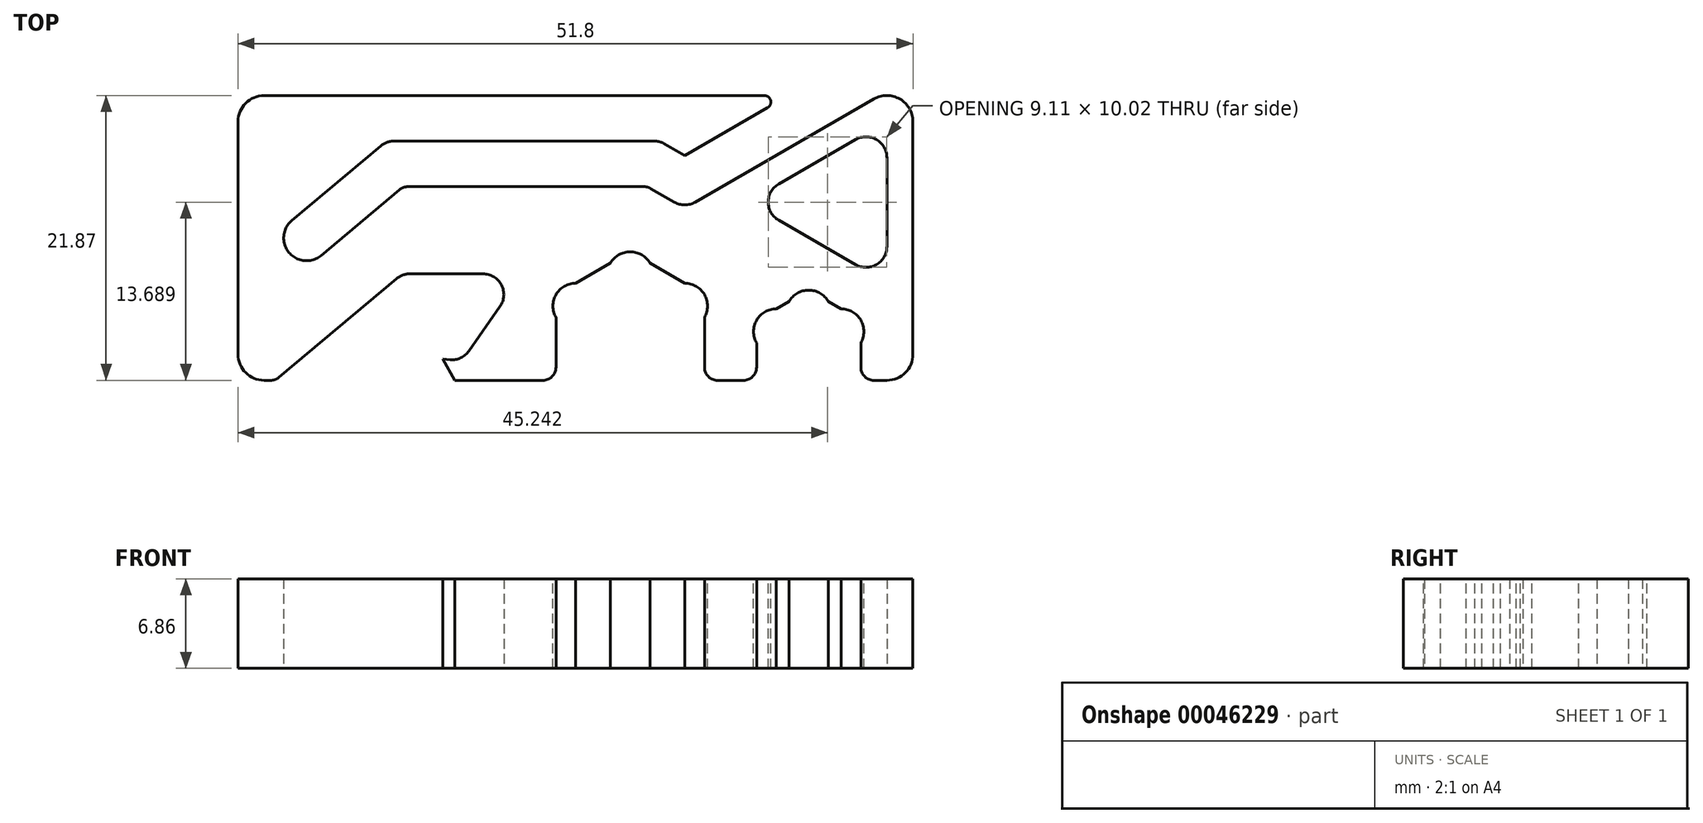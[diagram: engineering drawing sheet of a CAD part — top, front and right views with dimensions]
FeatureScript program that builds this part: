
annotation { "Feature Type Name" : "Feature", "Feature Type Description" : "" }
export const myFeature = defineFeature(function(context is Context, id is Id, definition is map)
    precondition{}
    {
        {
            var Q0;
            Q0=qCreatedBy(makeId("Top.planeOp"),FACE);
            var sketch = newSketch(context, id + "F0", { "sketchPlane" : qUnion([Q0])});
            skLineSegment(sketch, "E0", {"start": v(2, 0) * mm, "end": v(2.5, 0) * mm});
            skLineSegment(sketch, "E1", {"start": v(3.14, 0.23) * mm, "end": v(12.61, 8.18) * mm});
            skLineSegment(sketch, "E2", {"start": v(12.61, 8.18) * mm, "end": v(18.8, 8.18) * mm});
            skLineSegment(sketch, "E3", {"start": v(24.4, 0) * mm, "end": v(16.64, 0) * mm});
            skLineSegment(sketch, "E4", {"start": v(16.64, 0) * mm, "end": v(15.7, 1.63) * mm});
            skLineSegment(sketch, "E5", {"start": v(15.7, 1.63) * mm, "end": v(17.2, 1.5) * mm});
            skLineSegment(sketch, "E6", {"start": v(17.2, 1.5) * mm, "end": v(20.1, 5.66) * mm});
            skArc(sketch, "E7", {"start": v(20.1, 5.66) * mm, "mid": v(20.22, 7.32) * mm, "end": v(18.8, 8.18) * mm});
            skLineSegment(sketch, "E8", {"start": v(24.4, 0) * mm, "end": v(24.4, 6.58) * mm});
            skLineSegment(sketch, "E9", {"start": v(24.4, 6.58) * mm, "end": v(30.1, 9.87) * mm});
            skLineSegment(sketch, "E10", {"start": v(30.1, 9.87) * mm, "end": v(35.8, 6.58) * mm});
            skLineSegment(sketch, "E11", {"start": v(35.8, 6.58) * mm, "end": v(35.8, 0) * mm});
            skCircle(sketch, "E12", {"center": v(30.1, 3.3) * mm, "radius": 5.7 * mm, "construction": true});
            skLineSegment(sketch, "E13", {"start": v(18.8, 6.58) * mm, "end": v(20.4, 6.58) * mm, "construction": true});
            skArc(sketch, "E14", {"start": v(2.5, 0) * mm, "mid": v(2.84, 0.06) * mm, "end": v(3.14, 0.23) * mm});
            skLineSegment(sketch, "E15", {"start": v(0, 2) * mm, "end": v(0, 21.87) * mm});
            skArc(sketch, "E16", {"start": v(0, 2) * mm, "mid": v(0.59, 0.59) * mm, "end": v(2, 0) * mm});
            skLineSegment(sketch, "E17", {"start": v(35.8, 0) * mm, "end": v(39.8, 0) * mm});
            skLineSegment(sketch, "E18", {"start": v(39.8, 0) * mm, "end": v(39.8, 4.62) * mm});
            skLineSegment(sketch, "E19", {"start": v(39.8, 4.62) * mm, "end": v(43.8, 6.93) * mm});
            skLineSegment(sketch, "E20", {"start": v(43.8, 6.93) * mm, "end": v(47.8, 4.62) * mm});
            skLineSegment(sketch, "E21", {"start": v(47.8, 4.62) * mm, "end": v(47.8, 0) * mm});
            skLineSegment(sketch, "E22", {"start": v(47.8, 0) * mm, "end": v(51.8, 0) * mm});
            skCircle(sketch, "E23", {"center": v(43.8, 2.3) * mm, "radius": 4 * mm, "construction": true});
            skLineSegment(sketch, "E24", {"start": v(39.09, 13.69) * mm, "end": v(49.8, 7.5) * mm});
            skLineSegment(sketch, "E25", {"start": v(49.8, 7.5) * mm, "end": v(49.8, 19.87) * mm});
            skLineSegment(sketch, "E26", {"start": v(49.8, 19.87) * mm, "end": v(39.09, 13.69) * mm});
            skLineSegment(sketch, "E27", {"start": v(51.8, 0) * mm, "end": v(51.8, 19.87) * mm});
            skLineSegment(sketch, "E28", {"start": v(6.37, 9.6) * mm, "end": v(12.66, 14.87) * mm});
            skLineSegment(sketch, "E29", {"start": v(12.66, 14.87) * mm, "end": v(30.1, 14.87) * mm});
            skArc(sketch, "E30", {"start": v(4.13, 12.28) * mm, "mid": v(3.9, 9.81) * mm, "end": v(6.37, 9.6) * mm});
            skLineSegment(sketch, "E31", {"start": v(4.13, 12.28) * mm, "end": v(11.39, 18.37) * mm});
            skPoint(sketch, "E32", {"position": v(3.5, 10.94) * mm});
            skLineSegment(sketch, "E33", {"start": v(11.39, 18.37) * mm, "end": v(32.37, 18.37) * mm});
            skLineSegment(sketch, "E34", {"start": v(30.1, 14.87) * mm, "end": v(31.44, 14.87) * mm});
            skLineSegment(sketch, "E35", {"start": v(31.44, 14.87) * mm, "end": v(34.29, 13.23) * mm});
            skLineSegment(sketch, "E36", {"start": v(34.29, 13.23) * mm, "end": v(48.8, 21.6) * mm});
            skLineSegment(sketch, "E37", {"start": v(42.26, 21.87) * mm, "end": v(34.29, 17.27) * mm});
            skLineSegment(sketch, "E38", {"start": v(34.29, 17.27) * mm, "end": v(32.37, 18.37) * mm});
            skLineSegment(sketch, "E39", {"start": v(42.26, 21.87) * mm, "end": v(0, 21.87) * mm});
            skLineSegment(sketch, "E40", {"start": v(0, 0) * mm, "end": v(0, 21.87) * mm, "construction": true});
            skPoint(sketch, "E41", {"position": v(0, 10.94) * mm});
            skArc(sketch, "E42", {"start": v(51.8, 19.87) * mm, "mid": v(50.8, 21.6) * mm, "end": v(48.8, 21.6) * mm});
            skSolve(sketch);
        }
        {
            var Q0;
            Q0=makeQuery(id+"F0.imprint","IMPRINT",FACE,{"disambiguationData":[TD([[makeQuery(id+"F0.imprint","IMPRINT",EDGE,{"derivedFrom":sQuery(id+"F0.wireOp",EDGE,"E0")}),1.0]])]});
            extrude(context, id + "F1", {"entities" : qUnion([Q0]), "depth" : 6.86 * mm});
        }
        {
            var Q0;
            Q0=makeQuery(id+"F1.opExtrude","CAP_FACE",FACE,{"disambiguationData":[OSD([sQuery(id+"F0.wireOp",EDGE,"E0"),sQuery(id+"F0.wireOp",EDGE,"E1"),sQuery(id+"F0.wireOp",EDGE,"E2"),sQuery(id+"F0.wireOp",EDGE,"E3"),sQuery(id+"F0.wireOp",EDGE,"E4"),sQuery(id+"F0.wireOp",EDGE,"E5"),sQuery(id+"F0.wireOp",EDGE,"E6"),sQuery(id+"F0.wireOp",EDGE,"E7"),sQuery(id+"F0.wireOp",EDGE,"E8"),sQuery(id+"F0.wireOp",EDGE,"E9"),sQuery(id+"F0.wireOp",EDGE,"E10"),sQuery(id+"F0.wireOp",EDGE,"E11"),sQuery(id+"F0.wireOp",EDGE,"E14"),sQuery(id+"F0.wireOp",EDGE,"E15"),sQuery(id+"F0.wireOp",EDGE,"E16"),sQuery(id+"F0.wireOp",EDGE,"E17"),sQuery(id+"F0.wireOp",EDGE,"E18"),sQuery(id+"F0.wireOp",EDGE,"E19"),sQuery(id+"F0.wireOp",EDGE,"E20"),sQuery(id+"F0.wireOp",EDGE,"E21"),sQuery(id+"F0.wireOp",EDGE,"E22"),sQuery(id+"F0.wireOp",EDGE,"E24"),sQuery(id+"F0.wireOp",EDGE,"E25"),sQuery(id+"F0.wireOp",EDGE,"E26"),sQuery(id+"F0.wireOp",EDGE,"E27"),sQuery(id+"F0.wireOp",EDGE,"E28"),sQuery(id+"F0.wireOp",EDGE,"E29"),sQuery(id+"F0.wireOp",EDGE,"E30"),sQuery(id+"F0.wireOp",EDGE,"E31"),sQuery(id+"F0.wireOp",EDGE,"E33"),sQuery(id+"F0.wireOp",EDGE,"E34"),sQuery(id+"F0.wireOp",EDGE,"E35"),sQuery(id+"F0.wireOp",EDGE,"E36"),sQuery(id+"F0.wireOp",EDGE,"E37"),sQuery(id+"F0.wireOp",EDGE,"E38"),sQuery(id+"F0.wireOp",EDGE,"E39"),sQuery(id+"F0.wireOp",EDGE,"E42")])],"isStart":false});
            var sketch = newSketch(context, id + "F2", { "sketchPlane" : qUnion([Q0])});
            skLineSegment(sketch, "E43", {"start": v(30.1, 9.87) * mm, "end": v(30.1, 3.3) * mm, "construction": true});
            skLineSegment(sketch, "E44", {"start": v(30.1, 3.3) * mm, "end": v(24.4, 6.58) * mm, "construction": true});
            skLineSegment(sketch, "E45", {"start": v(30.1, 3.3) * mm, "end": v(35.8, 6.58) * mm, "construction": true});
            skCircle(sketch, "E46", {"center": v(30.1, 8.12) * mm, "radius": 1.75 * mm});
            skCircle(sketch, "E47", {"center": v(34.28, 5.7) * mm, "radius": 1.75 * mm});
            skCircle(sketch, "E48", {"center": v(25.91, 5.7) * mm, "radius": 1.75 * mm});
            skLineSegment(sketch, "E49", {"start": v(43.8, 6.93) * mm, "end": v(43.8, 2.3) * mm, "construction": true});
            skLineSegment(sketch, "E50", {"start": v(43.8, 2.3) * mm, "end": v(39.8, 4.62) * mm, "construction": true});
            skLineSegment(sketch, "E51", {"start": v(43.8, 2.3) * mm, "end": v(47.8, 4.62) * mm, "construction": true});
            skCircle(sketch, "E52", {"center": v(43.8, 5.18) * mm, "radius": 1.75 * mm});
            skCircle(sketch, "E53", {"center": v(46.28, 3.74) * mm, "radius": 1.75 * mm});
            skCircle(sketch, "E54", {"center": v(41.31, 3.74) * mm, "radius": 1.75 * mm});
            skLineSegment(sketch, "E55", {"start": v(21.88, 18.37) * mm, "end": v(21.88, 14.87) * mm, "construction": true});
            skLineSegment(sketch, "E56", {"start": v(28.35, 8.12) * mm, "end": v(31.85, 8.12) * mm, "construction": true});
            skSolve(sketch);
        }
        {
            var Q0;
            Q0 = qSketchRegion(id + "F2", true);
            extrude(context, id + "F3", {"entities" : qUnion([Q0]), "operationType" : NewBodyOperationType.REMOVE, "endBound" : BoundingType.THROUGH_ALL, "oppositeDirection" : true, "depth" : 25 * mm});
        }
        {
            var Q0;
            Q0=makeQuery(id+"F1.opExtrude","SWEPT_EDGE",EDGE,{"disambiguationData":[OSD([sQuery(id+"F0.wireOp",EDGE,"E3"),sQuery(id+"F0.wireOp",EDGE,"E8")])]});
            var Q1;
            Q1=makeQuery(id+"F1.opExtrude","SWEPT_EDGE",EDGE,{"disambiguationData":[OSD([sQuery(id+"F0.wireOp",EDGE,"E11"),sQuery(id+"F0.wireOp",EDGE,"E17")])]});
            var Q2;
            Q2=makeQuery(id+"F1.opExtrude","SWEPT_EDGE",EDGE,{"disambiguationData":[OSD([sQuery(id+"F0.wireOp",EDGE,"E17"),sQuery(id+"F0.wireOp",EDGE,"E18")])]});
            var Q3;
            Q3=makeQuery(id+"F1.opExtrude","SWEPT_EDGE",EDGE,{"disambiguationData":[OSD([sQuery(id+"F0.wireOp",EDGE,"E21"),sQuery(id+"F0.wireOp",EDGE,"E22")])]});
            fillet(context, id + "F4", {"entities" : qUnion([Q0, Q1, Q2, Q3]), "radius" : 1 * mm, "tangentPropagation" : true, "allowEdgeOverflow" : false});
        }
        {
            var Q0;
            Q0=makeQuery(id+"F1.opExtrude","SWEPT_EDGE",EDGE,{"disambiguationData":[OSD([sQuery(id+"F0.wireOp",EDGE,"E22"),sQuery(id+"F0.wireOp",EDGE,"E27")])]});
            var Q1;
            Q1=makeQuery(id+"F1.opExtrude","SWEPT_EDGE",EDGE,{"disambiguationData":[OSD([sQuery(id+"F0.wireOp",EDGE,"E15"),sQuery(id+"F0.wireOp",EDGE,"E39")])]});
            fillet(context, id + "F5", {"entities" : qUnion([Q0, Q1]), "radius" : 2 * mm, "tangentPropagation" : true, "allowEdgeOverflow" : false});
        }
        {
            var Q0;
            Q0=makeQuery(id+"F1.opExtrude","SWEPT_EDGE",EDGE,{"disambiguationData":[OSD([sQuery(id+"F0.wireOp",EDGE,"E37"),sQuery(id+"F0.wireOp",EDGE,"E39")])]});
            fillet(context, id + "F6", {"entities" : qUnion([Q0]), "radius" : 0.5 * mm, "tangentPropagation" : true, "allowEdgeOverflow" : false});
        }
        {
            var Q0;
            Q0=makeQuery(id+"F1.opExtrude","SWEPT_EDGE",EDGE,{"disambiguationData":[OSD([sQuery(id+"F0.wireOp",EDGE,"E28"),sQuery(id+"F0.wireOp",EDGE,"E29")])]});
            var Q1;
            Q1=makeQuery(id+"F1.opExtrude","SWEPT_EDGE",EDGE,{"disambiguationData":[OSD([sQuery(id+"F0.wireOp",EDGE,"E34"),sQuery(id+"F0.wireOp",EDGE,"E35")])]});
            fillet(context, id + "F7", {"entities" : qUnion([Q0, Q1]), "radius" : 1 * mm, "tangentPropagation" : true, "allowEdgeOverflow" : false});
        }
        {
            var Q0;
            Q0=makeQuery(id+"F1.opExtrude","SWEPT_EDGE",EDGE,{"disambiguationData":[OSD([sQuery(id+"F0.wireOp",EDGE,"E24"),sQuery(id+"F0.wireOp",EDGE,"E26")])]});
            var Q1;
            Q1=makeQuery(id+"F1.opExtrude","SWEPT_EDGE",EDGE,{"disambiguationData":[OSD([sQuery(id+"F0.wireOp",EDGE,"E25"),sQuery(id+"F0.wireOp",EDGE,"E26")])]});
            var Q2;
            Q2=makeQuery(id+"F1.opExtrude","SWEPT_EDGE",EDGE,{"disambiguationData":[OSD([sQuery(id+"F0.wireOp",EDGE,"E24"),sQuery(id+"F0.wireOp",EDGE,"E25")])]});
            fillet(context, id + "F8", {"entities" : qUnion([Q0, Q1, Q2]), "radius" : 1.6 * mm, "tangentPropagation" : true, "allowEdgeOverflow" : false});
        }
        {
            var Q0;
            Q0=makeQuery(id+"F1.opExtrude","SWEPT_EDGE",EDGE,{"disambiguationData":[OSD([sQuery(id+"F0.wireOp",EDGE,"E5"),sQuery(id+"F0.wireOp",EDGE,"E6")])]});
            fillet(context, id + "F9", {"entities" : qUnion([Q0]), "radius" : 1.6 * mm, "tangentPropagation" : true, "allowEdgeOverflow" : false});
        }
        {
            var Q0;
            Q0=makeQuery(id+"F1.opExtrude","SWEPT_EDGE",EDGE,{"disambiguationData":[OSD([sQuery(id+"F0.wireOp",EDGE,"E35"),sQuery(id+"F0.wireOp",EDGE,"E36")])]});
            var Q1;
            Q1=makeQuery(id+"F1.opExtrude","SWEPT_EDGE",EDGE,{"disambiguationData":[OSD([sQuery(id+"F0.wireOp",EDGE,"E33"),sQuery(id+"F0.wireOp",EDGE,"E38")])]});
            var Q2;
            Q2=makeQuery(id+"F1.opExtrude","SWEPT_EDGE",EDGE,{"disambiguationData":[OSD([sQuery(id+"F0.wireOp",EDGE,"E31"),sQuery(id+"F0.wireOp",EDGE,"E33")])]});
            var Q3;
            Q3=makeQuery(id+"F1.opExtrude","SWEPT_EDGE",EDGE,{"disambiguationData":[OSD([sQuery(id+"F0.wireOp",EDGE,"E1"),sQuery(id+"F0.wireOp",EDGE,"E2")])]});
            fillet(context, id + "F10", {"entities" : qUnion([Q0, Q1, Q2, Q3]), "radius" : 1.6 * mm, "tangentPropagation" : true, "allowEdgeOverflow" : false});
        }
    });
